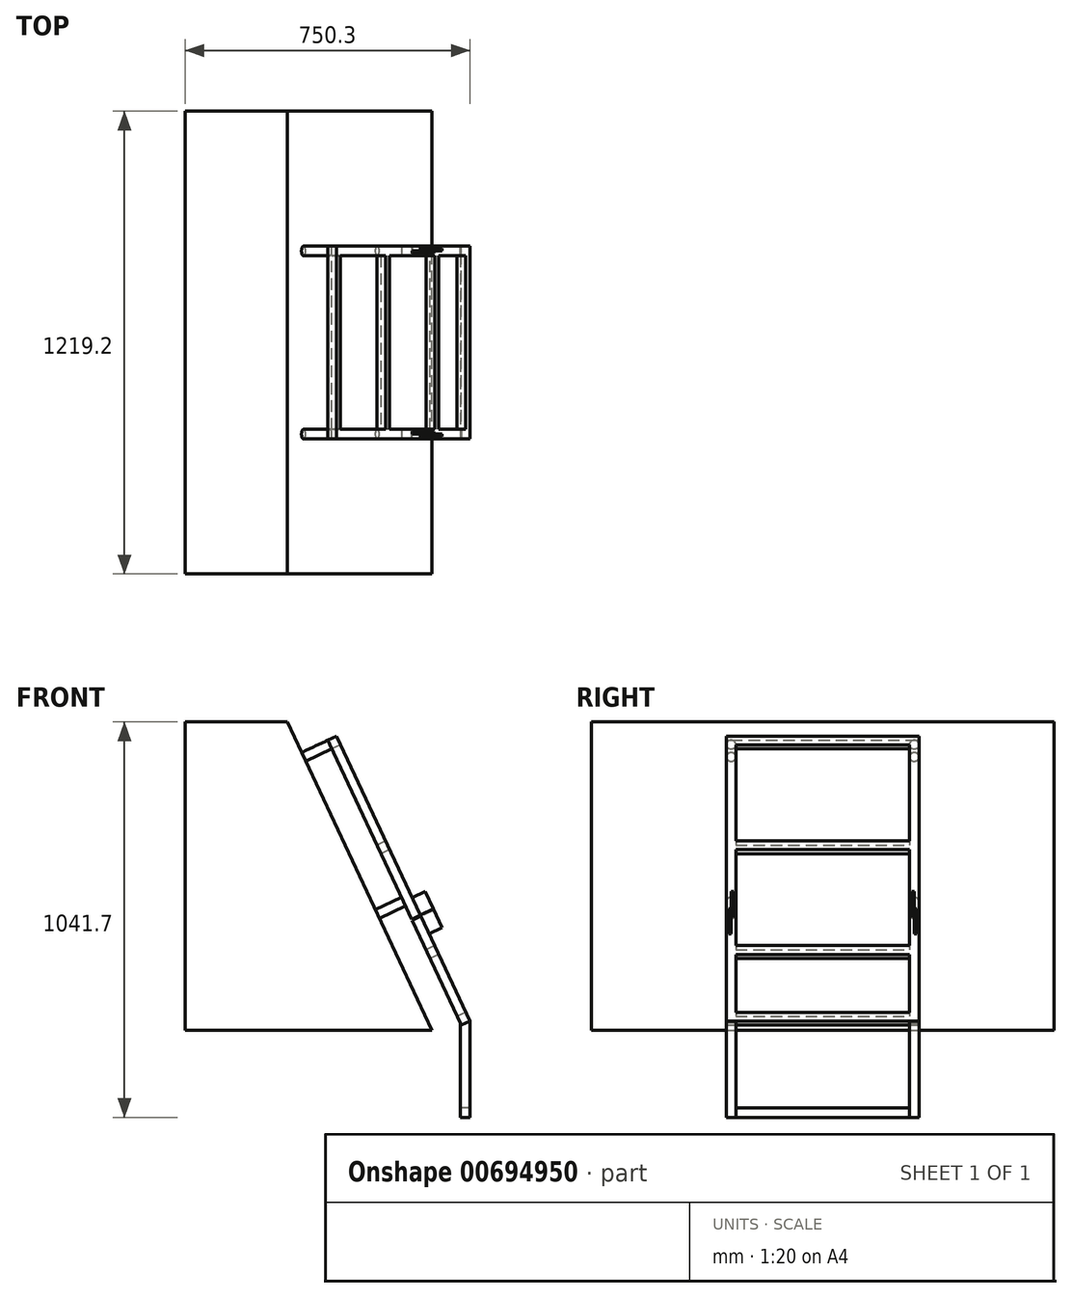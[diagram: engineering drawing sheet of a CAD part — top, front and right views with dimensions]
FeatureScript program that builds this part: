
annotation { "Feature Type Name" : "Feature", "Feature Type Description" : "" }
export const myFeature = defineFeature(function(context is Context, id is Id, definition is map)
    precondition{}
    {
        {
            var Q0;
            Q0=qCreatedBy(makeId("Front.planeOp"),FACE);
            var sketch = newSketch(context, id + "F0", { "sketchPlane" : qUnion([Q0])});
            skLineSegment(sketch, "E0", {"start": v(0, 0) * mm, "end": v(0, 812.8) * mm});
            skLineSegment(sketch, "E1", {"start": v(0, 812.8) * mm, "end": v(-381, 812.8) * mm});
            skLineSegment(sketch, "E2", {"start": v(-381, 812.8) * mm, "end": v(0, 0) * mm});
            skLineSegment(sketch, "E3", {"start": v(0, 0) * mm, "end": v(0, -325.78) * mm});
            skLineSegment(sketch, "E4", {"start": v(-381, 812.8) * mm, "end": v(-649.86, 812.8) * mm});
            skLineSegment(sketch, "E5", {"start": v(-649.86, 812.8) * mm, "end": v(-649.86, 0) * mm});
            skLineSegment(sketch, "E6", {"start": v(-649.86, 0) * mm, "end": v(0, 0) * mm});
            skSolve(sketch);
        }
        {
            var Q0;
            Q0=makeQuery(id+"F0.imprint","IMPRINT",FACE,{"disambiguationData":[TD([[makeQuery(id+"F0.imprint","IMPRINT",EDGE,{"derivedFrom":sQuery(id+"F0.wireOp",EDGE,"E2")}),-1.0]])]});
            extrude(context, id + "F1", {"entities" : qUnion([Q0]), "endBound" : BoundingType.SYMMETRIC, "depth" : 1219.2 * mm, "offsetDistance" : 25.4 * mm});
        }
        {
            var Q0;
            Q0=makeQuery(id+"F1.opExtrude","SWEPT_FACE",FACE,{"disambiguationData":[OSD([sQuery(id+"F0.wireOp",EDGE,"E2")])]});
            var sketch = newSketch(context, id + "F2", { "sketchPlane" : qUnion([Q0])});
            skCircle(sketch, "E7", {"center": v(-241.3, 796.07) * mm, "radius": 12.7 * mm});
            skCircle(sketch, "E8", {"center": v(241.3, 796.07) * mm, "radius": 12.7 * mm});
            skCircle(sketch, "E9", {"center": v(-241.3, 338.87) * mm, "radius": 12.7 * mm});
            skCircle(sketch, "E10", {"center": v(241.3, 338.87) * mm, "radius": 12.7 * mm});
            skSolve(sketch);
        }
        {
            var Q0;
            Q0=makeQuery(id+"F2.imprint","IMPRINT",FACE,{"disambiguationData":[TD([[makeQuery(id+"F2.imprint","IMPRINT",EDGE,{"derivedFrom":sQuery(id+"F2.wireOp",EDGE,"E7")}),1.0]])]});
            var Q1;
            Q1=makeQuery(id+"F2.imprint","IMPRINT",FACE,{"disambiguationData":[TD([[makeQuery(id+"F2.imprint","IMPRINT",EDGE,{"derivedFrom":sQuery(id+"F2.wireOp",EDGE,"E8")}),1.0]])]});
            var Q2;
            Q2=makeQuery(id+"F2.imprint","IMPRINT",FACE,{"disambiguationData":[TD([[makeQuery(id+"F2.imprint","IMPRINT",EDGE,{"derivedFrom":sQuery(id+"F2.wireOp",EDGE,"E10")}),1.0]])]});
            var Q3;
            Q3=makeQuery(id+"F2.imprint","IMPRINT",FACE,{"disambiguationData":[TD([[makeQuery(id+"F2.imprint","IMPRINT",EDGE,{"derivedFrom":sQuery(id+"F2.wireOp",EDGE,"E9")}),1.0]])]});
            extrude(context, id + "F3", {"entities" : qUnion([Q0, Q1, Q2, Q3]), "operationType" : NewBodyOperationType.ADD, "depth" : 76.2 * mm, "offsetDistance" : 25.4 * mm});
        }
        {
            var Q0;
            Q0=makeQuery(id+"F3.opExtrude","CAP_FACE",FACE,{"disambiguationData":[OSD([sQuery(id+"F2.wireOp",EDGE,"E9")])],"isStart":false});
            var sketch = newSketch(context, id + "F4", { "sketchPlane" : qUnion([Q0])});
            skCircle(sketch, "E11.0", {"center": v(-241.3, 796.07) * mm, "radius": 12.7 * mm});
            skCircle(sketch, "E12.0", {"center": v(241.3, 796.07) * mm, "radius": 12.7 * mm});
            skCircle(sketch, "E13.0.0", {"center": v(241.3, 338.87) * mm, "radius": 12.7 * mm});
            skLineSegment(sketch, "E14", {"start": v(-241.3, 796.07) * mm, "end": v(-241.3, 288.07) * mm});
            skLineSegment(sketch, "E15", {"start": v(-241.3, 796.07) * mm, "end": v(241.3, 796.07) * mm});
            skLineSegment(sketch, "E16", {"start": v(241.3, 796.07) * mm, "end": v(241.3, 288.07) * mm});
            skLineSegment(sketch, "E17.0", {"start": v(-254, 808.77) * mm, "end": v(-254, 288.07) * mm});
            skLineSegment(sketch, "E17.1", {"start": v(-254, 808.77) * mm, "end": v(254, 808.77) * mm});
            skLineSegment(sketch, "E17.2", {"start": v(254, 808.77) * mm, "end": v(254, 288.07) * mm});
            skLineSegment(sketch, "E18.0", {"start": v(-228.6, 783.37) * mm, "end": v(-228.6, 288.07) * mm});
            skLineSegment(sketch, "E18.1", {"start": v(-228.6, 783.37) * mm, "end": v(228.6, 783.37) * mm});
            skLineSegment(sketch, "E18.2", {"start": v(228.6, 783.37) * mm, "end": v(228.6, 288.07) * mm});
            skLineSegment(sketch, "E19", {"start": v(-254, 288.07) * mm, "end": v(-228.6, 288.07) * mm});
            skLineSegment(sketch, "E20", {"start": v(254, 288.07) * mm, "end": v(228.6, 288.07) * mm});
            skLineSegment(sketch, "E21", {"start": v(-228.6, 503.97) * mm, "end": v(228.6, 503.97) * mm});
            skLineSegment(sketch, "E22", {"start": v(228.6, 503.97) * mm, "end": v(228.6, 478.57) * mm});
            skLineSegment(sketch, "E23", {"start": v(228.6, 478.57) * mm, "end": v(-228.6, 478.57) * mm});
            skLineSegment(sketch, "E24", {"start": v(-228.6, 478.57) * mm, "end": v(-228.6, 503.97) * mm});
            skLineSegment(sketch, "E25", {"start": v(-254, 284.9) * mm, "end": v(-228.6, 284.9) * mm});
            skLineSegment(sketch, "E26", {"start": v(-228.6, 284.9) * mm, "end": v(-228.6, -19.9) * mm});
            skLineSegment(sketch, "E27", {"start": v(-254, 284.9) * mm, "end": v(-254, -19.9) * mm});
            skLineSegment(sketch, "E28", {"start": v(-254, -19.9) * mm, "end": v(-228.6, -19.9) * mm});
            skLineSegment(sketch, "E29.bottom", {"start": v(254, 284.9) * mm, "end": v(228.6, 284.9) * mm});
            skLineSegment(sketch, "E29.top", {"start": v(254, -19.9) * mm, "end": v(228.6, -19.9) * mm});
            skLineSegment(sketch, "E29.left", {"start": v(254, 284.9) * mm, "end": v(254, -19.9) * mm});
            skLineSegment(sketch, "E29.right", {"start": v(228.6, 284.9) * mm, "end": v(228.6, -19.9) * mm});
            skLineSegment(sketch, "E30.bottom", {"start": v(-228.6, 199.17) * mm, "end": v(228.6, 199.17) * mm});
            skLineSegment(sketch, "E30.top", {"start": v(-228.6, 173.77) * mm, "end": v(228.6, 173.77) * mm});
            skLineSegment(sketch, "E30.left", {"start": v(-228.6, 199.17) * mm, "end": v(-228.6, 173.77) * mm});
            skLineSegment(sketch, "E30.right", {"start": v(228.6, 199.17) * mm, "end": v(228.6, 173.77) * mm});
            skLineSegment(sketch, "E31.bottom", {"start": v(-228.6, -19.9) * mm, "end": v(228.6, -19.9) * mm});
            skLineSegment(sketch, "E31.top", {"start": v(-228.6, 5.5) * mm, "end": v(228.6, 5.5) * mm});
            skLineSegment(sketch, "E31.left", {"start": v(-228.6, -19.9) * mm, "end": v(-228.6, 5.5) * mm});
            skLineSegment(sketch, "E31.right", {"start": v(228.6, -19.9) * mm, "end": v(228.6, 5.5) * mm});
            skSolve(sketch);
        }
        {
            var Q0;
            {var subQ5=sQuery(id+"F4.wireOp",EDGE,"E18.1");Q0=makeQuery(id+"F4.imprint","IMPRINT",FACE,{"disambiguationData":[TD([[makeQuery(id+"F4.imprint","IMPRINT",EDGE,{"derivedFrom":subQ5}),1.0]])]});}
            var Q1;
            {var subQ0=sQuery(id+"F4.wireOp",EDGE,"E17.1");var subQ1=sQuery(id+"F4.wireOp",EDGE,"E11.0");var subQ2=makeQuery(id+"F4.imprint","INTERSECT",VERTEX,{"derivedFrom":[subQ1,subQ0]});Q1=makeQuery(id+"F4.imprint","IMPRINT",FACE,{"disambiguationData":[TD([[makeQuery(id+"F4.imprint","IMPRINT",EDGE,{"disambiguationData":[TD([[subQ2,1.0]])],"derivedFrom":subQ1}),-1.0]])]});}
            var Q2;
            {var subQ0=sQuery(id+"F4.wireOp",EDGE,"E17.0");var subQ1=sQuery(id+"F4.wireOp",EDGE,"E11.0");var subQ2=makeQuery(id+"F4.imprint","INTERSECT",VERTEX,{"derivedFrom":[subQ1,subQ0]});Q2=makeQuery(id+"F4.imprint","IMPRINT",FACE,{"disambiguationData":[TD([[makeQuery(id+"F4.imprint","IMPRINT",EDGE,{"disambiguationData":[TD([[subQ2,-1.0]])],"derivedFrom":subQ1}),-1.0]])]});}
            var Q3;
            {var subQ0=sQuery(id+"F4.wireOp",EDGE,"E17.2");var subQ1=sQuery(id+"F4.wireOp",EDGE,"E12.0");var subQ2=makeQuery(id+"F4.imprint","INTERSECT",VERTEX,{"derivedFrom":[subQ1,subQ0]});Q3=makeQuery(id+"F4.imprint","IMPRINT",FACE,{"disambiguationData":[TD([[makeQuery(id+"F4.imprint","IMPRINT",EDGE,{"disambiguationData":[TD([[subQ2,1.0]])],"derivedFrom":subQ1}),-1.0]])]});}
            var Q4;
            {var subQ3=sQuery(id+"F4.wireOp",EDGE,"E12.0");var subQ7=makeQuery(id+"F4.imprint","INTERSECT",VERTEX,{"derivedFrom":[subQ3,sQuery(id+"F4.wireOp",EDGE,"E17.1")]});Q4=makeQuery(id+"F4.imprint","IMPRINT",FACE,{"disambiguationData":[TD([[makeQuery(id+"F4.imprint","IMPRINT",EDGE,{"disambiguationData":[TD([[subQ7,1.0]])],"derivedFrom":subQ3}),1.0]])]});}
            var Q5;
            {var subQ0=sQuery(id+"F4.wireOp",EDGE,"E15");var subQ1=sQuery(id+"F4.wireOp",EDGE,"E12.0");var subQ2=makeQuery(id+"F4.imprint","INTERSECT",VERTEX,{"derivedFrom":[subQ1,subQ0]});Q5=makeQuery(id+"F4.imprint","IMPRINT",FACE,{"disambiguationData":[TD([[makeQuery(id+"F4.imprint","IMPRINT",EDGE,{"disambiguationData":[TD([[subQ2,-1.0]])],"derivedFrom":subQ1}),1.0]])]});}
            var Q6;
            {var subQ0=sQuery(id+"F4.wireOp",EDGE,"E17.1");var subQ1=sQuery(id+"F4.wireOp",EDGE,"E12.0");var subQ2=makeQuery(id+"F4.imprint","INTERSECT",VERTEX,{"derivedFrom":[subQ1,subQ0]});Q6=makeQuery(id+"F4.imprint","IMPRINT",FACE,{"disambiguationData":[TD([[makeQuery(id+"F4.imprint","IMPRINT",EDGE,{"disambiguationData":[TD([[subQ2,1.0]])],"derivedFrom":subQ1}),-1.0]])]});}
            var Q7;
            {var subQ3=sQuery(id+"F4.wireOp",EDGE,"E11.0");var subQ5=makeQuery(id+"F4.imprint","INTERSECT",VERTEX,{"derivedFrom":[subQ3,sQuery(id+"F4.wireOp",EDGE,"E17.1")]});Q7=makeQuery(id+"F4.imprint","IMPRINT",FACE,{"disambiguationData":[TD([[makeQuery(id+"F4.imprint","IMPRINT",EDGE,{"disambiguationData":[TD([[subQ5,1.0]])],"derivedFrom":subQ3}),1.0]])]});}
            var Q8;
            {var subQ0=sQuery(id+"F4.wireOp",EDGE,"E17.1");var subQ1=sQuery(id+"F4.wireOp",EDGE,"E11.0");var subQ2=makeQuery(id+"F4.imprint","INTERSECT",VERTEX,{"derivedFrom":[subQ1,subQ0]});Q8=makeQuery(id+"F4.imprint","IMPRINT",FACE,{"disambiguationData":[TD([[makeQuery(id+"F4.imprint","IMPRINT",EDGE,{"disambiguationData":[TD([[subQ2,-1.0]])],"derivedFrom":subQ1}),-1.0]])]});}
            var Q9;
            {var subQ0=sQuery(id+"F4.wireOp",EDGE,"E15");var subQ1=sQuery(id+"F4.wireOp",EDGE,"E11.0");var subQ2=makeQuery(id+"F4.imprint","INTERSECT",VERTEX,{"derivedFrom":[subQ1,subQ0]});Q9=makeQuery(id+"F4.imprint","IMPRINT",FACE,{"disambiguationData":[TD([[makeQuery(id+"F4.imprint","IMPRINT",EDGE,{"disambiguationData":[TD([[subQ2,1.0]])],"derivedFrom":subQ1}),1.0]])]});}
            var Q10;
            Q10=makeQuery(id+"F4.imprint","IMPRINT",FACE,{"disambiguationData":[TD([[makeQuery(id+"F4.imprint","IMPRINT",EDGE,{"derivedFrom":sQuery(id+"F4.wireOp",EDGE,"E21")}),-1.0]])]});
            var Q11;
            {var subQ0=sQuery(id+"F4.wireOp",EDGE,"E14");var subQ1=makeQuery(id+"F3.opExtrude","CAP_EDGE",EDGE,{"disambiguationData":[OSD([sQuery(id+"F2.wireOp",EDGE,"E9")])],"isStart":false});var subQ2=makeQuery(id+"F4.imprint","INTERSECT",VERTEX,{"disambiguationData":[OD(0.0)],"derivedFrom":[subQ1,subQ0]});Q11=makeQuery(id+"F4.imprint","IMPRINT",FACE,{"disambiguationData":[TD([[makeQuery(id+"F4.imprint","IMPRINT",EDGE,{"disambiguationData":[TD([[subQ2,-1.0]])],"derivedFrom":subQ0}),-1.0]])]});}
            var Q12;
            {var subQ0=sQuery(id+"F4.wireOp",EDGE,"E14");var subQ1=makeQuery(id+"F3.opExtrude","CAP_EDGE",EDGE,{"disambiguationData":[OSD([sQuery(id+"F2.wireOp",EDGE,"E9")])],"isStart":false});var subQ2=makeQuery(id+"F4.imprint","INTERSECT",VERTEX,{"disambiguationData":[OD(0.0)],"derivedFrom":[subQ1,subQ0]});Q12=makeQuery(id+"F4.imprint","IMPRINT",FACE,{"disambiguationData":[TD([[makeQuery(id+"F4.imprint","IMPRINT",EDGE,{"disambiguationData":[TD([[subQ2,-1.0]])],"derivedFrom":subQ0}),1.0]])]});}
            var Q13;
            {var subQ0=sQuery(id+"F4.wireOp",EDGE,"E19");var subQ1=sQuery(id+"F4.wireOp",EDGE,"E14");var subQ2=makeQuery(id+"F4.imprint","INTERSECT",VERTEX,{"derivedFrom":[subQ1,subQ0]});Q13=makeQuery(id+"F4.imprint","IMPRINT",FACE,{"disambiguationData":[TD([[makeQuery(id+"F4.imprint","IMPRINT",EDGE,{"disambiguationData":[TD([[subQ2,1.0]])],"derivedFrom":subQ1}),1.0]])]});}
            var Q14;
            {var subQ0=sQuery(id+"F4.wireOp",EDGE,"E19");var subQ1=sQuery(id+"F4.wireOp",EDGE,"E14");var subQ2=makeQuery(id+"F4.imprint","INTERSECT",VERTEX,{"derivedFrom":[subQ1,subQ0]});Q14=makeQuery(id+"F4.imprint","IMPRINT",FACE,{"disambiguationData":[TD([[makeQuery(id+"F4.imprint","IMPRINT",EDGE,{"disambiguationData":[TD([[subQ2,1.0]])],"derivedFrom":subQ1}),-1.0]])]});}
            var Q15;
            {var subQ3=sQuery(id+"F4.wireOp",EDGE,"E25");Q15=makeQuery(id+"F4.imprint","IMPRINT",FACE,{"disambiguationData":[TD([[makeQuery(id+"F4.imprint","IMPRINT",EDGE,{"derivedFrom":subQ3}),-1.0]])]});}
            var Q16;
            {var subQ0=sQuery(id+"F4.wireOp",EDGE,"E13.0.0");var subQ1=makeQuery(id+"F4.imprint","INTERSECT",VERTEX,{"derivedFrom":[subQ0,sQuery(id+"F4.wireOp",EDGE,"E17.2")]});Q16=makeQuery(id+"F4.imprint","IMPRINT",FACE,{"disambiguationData":[TD([[makeQuery(id+"F4.imprint","IMPRINT",EDGE,{"disambiguationData":[TD([[subQ1,-1.0]])],"derivedFrom":subQ0}),1.0]])]});}
            var Q17;
            {var subQ0=sQuery(id+"F4.wireOp",EDGE,"E13.0.0");var subQ1=makeQuery(id+"F4.imprint","INTERSECT",VERTEX,{"derivedFrom":[subQ0,sQuery(id+"F4.wireOp",EDGE,"E18.2")]});Q17=makeQuery(id+"F4.imprint","IMPRINT",FACE,{"disambiguationData":[TD([[makeQuery(id+"F4.imprint","IMPRINT",EDGE,{"disambiguationData":[TD([[subQ1,1.0]])],"derivedFrom":subQ0}),1.0]])]});}
            var Q18;
            {var subQ0=sQuery(id+"F4.wireOp",EDGE,"E18.2");var subQ1=sQuery(id+"F4.wireOp",EDGE,"E13.0.0");var subQ2=makeQuery(id+"F4.imprint","INTERSECT",VERTEX,{"derivedFrom":[subQ1,subQ0]});Q18=makeQuery(id+"F4.imprint","IMPRINT",FACE,{"disambiguationData":[TD([[makeQuery(id+"F4.imprint","IMPRINT",EDGE,{"disambiguationData":[TD([[subQ2,-1.0]])],"derivedFrom":subQ1}),-1.0]])]});}
            var Q19;
            {var subQ0=sQuery(id+"F4.wireOp",EDGE,"E17.2");var subQ1=sQuery(id+"F4.wireOp",EDGE,"E13.0.0");var subQ2=makeQuery(id+"F4.imprint","INTERSECT",VERTEX,{"derivedFrom":[subQ1,subQ0]});Q19=makeQuery(id+"F4.imprint","IMPRINT",FACE,{"disambiguationData":[TD([[makeQuery(id+"F4.imprint","IMPRINT",EDGE,{"disambiguationData":[TD([[subQ2,1.0]])],"derivedFrom":subQ1}),-1.0]])]});}
            var Q20;
            {var subQ1=sQuery(id+"F4.wireOp",EDGE,"E29.bottom");Q20=makeQuery(id+"F4.imprint","IMPRINT",FACE,{"disambiguationData":[TD([[makeQuery(id+"F4.imprint","IMPRINT",EDGE,{"derivedFrom":subQ1}),1.0]])]});}
            var Q21;
            Q21=makeQuery(id+"F4.imprint","IMPRINT",FACE,{"disambiguationData":[TD([[makeQuery(id+"F4.imprint","IMPRINT",EDGE,{"derivedFrom":sQuery(id+"F4.wireOp",EDGE,"E30.bottom")}),-1.0]])]});
            var Q22;
            Q22=makeQuery(id+"F4.imprint","IMPRINT",FACE,{"disambiguationData":[TD([[makeQuery(id+"F4.imprint","IMPRINT",EDGE,{"derivedFrom":sQuery(id+"F4.wireOp",EDGE,"E31.bottom")}),1.0]])]});
            extrude(context, id + "F5", {"entities" : qUnion([Q0, Q1, Q2, Q3, Q4, Q5, Q6, Q7, Q8, Q9, Q10, Q11, Q12, Q13, Q14, Q15, Q16, Q17, Q18, Q19, Q20, Q21, Q22]), "operationType" : NewBodyOperationType.ADD, "depth" : 25.4 * mm, "offsetDistance" : 25.4 * mm});
        }
        {
            var Q0;
            Q0=makeQuery(id+"F5.opExtrude","SWEPT_FACE",FACE,{"disambiguationData":[OSD([sQuery(id+"F4.wireOp",EDGE,"E27")])]});
            var sketch = newSketch(context, id + "F6", { "sketchPlane" : qUnion([Q0])});
            skLineSegment(sketch, "E32", {"start": v(100.44, 25.1) * mm, "end": v(100.44, -228.9) * mm});
            skLineSegment(sketch, "E33", {"start": v(75.04, -228.9) * mm, "end": v(100.44, -228.9) * mm});
            skLineSegment(sketch, "E34", {"start": v(75.04, -228.9) * mm, "end": v(75.04, 19.44) * mm});
            skSolve(sketch);
        }
        {
            var Q0;
            Q0=makeQuery(id+"F6.imprint","IMPRINT",FACE,{"disambiguationData":[TD([[makeQuery(id+"F6.imprint","IMPRINT",EDGE,{"derivedFrom":sQuery(id+"F6.wireOp",EDGE,"E32")}),-1.0]])]});
            extrude(context, id + "F7", {"entities" : qUnion([Q0]), "oppositeDirection" : true, "depth" : 25.4 * mm, "offsetDistance" : 25.4 * mm});
        }
        {
            var Q0;
            Q0=makeQuery(id+"F5.opExtrude","SWEPT_FACE",FACE,{"disambiguationData":[OSD([sQuery(id+"F4.wireOp",EDGE,"E29.left")])]});
            var sketch = newSketch(context, id + "F8", { "sketchPlane" : qUnion([Q0])});
            skLineSegment(sketch, "E35", {"start": v(-100.44, 25.1) * mm, "end": v(-100.44, -228.9) * mm});
            skLineSegment(sketch, "E36", {"start": v(-100.44, -228.9) * mm, "end": v(-75.04, -228.9) * mm});
            skLineSegment(sketch, "E37", {"start": v(-75.04, -228.9) * mm, "end": v(-75.04, 19.44) * mm});
            skSolve(sketch);
        }
        {
            var Q0;
            Q0=makeQuery(id+"F8.imprint","IMPRINT",FACE,{"disambiguationData":[TD([[makeQuery(id+"F8.imprint","IMPRINT",EDGE,{"derivedFrom":sQuery(id+"F8.wireOp",EDGE,"E35")}),1.0]])]});
            extrude(context, id + "F9", {"entities" : qUnion([Q0]), "oppositeDirection" : true, "depth" : 25.4 * mm, "offsetDistance" : 25.4 * mm});
        }
        {
            var Q0;
            Q0=makeQuery(id+"F7.opExtrude","CAP_FACE",FACE,{"disambiguationData":[OSD([sQuery(id+"F4.wireOp",EDGE,"E27"),sQuery(id+"F4.wireOp",EDGE,"E28"),sQuery(id+"F6.wireOp",EDGE,"E32"),sQuery(id+"F6.wireOp",EDGE,"E33"),sQuery(id+"F6.wireOp",EDGE,"E34")])],"isStart":false});
            var sketch = newSketch(context, id + "F10", { "sketchPlane" : qUnion([Q0])});
            skLineSegment(sketch, "E38.bottom", {"start": v(-100.44, -228.9) * mm, "end": v(-75.04, -228.9) * mm});
            skLineSegment(sketch, "E38.top", {"start": v(-100.44, -203.5) * mm, "end": v(-75.04, -203.5) * mm});
            skLineSegment(sketch, "E38.left", {"start": v(-100.44, -228.9) * mm, "end": v(-100.44, -203.5) * mm});
            skLineSegment(sketch, "E38.right", {"start": v(-75.04, -228.9) * mm, "end": v(-75.04, -203.5) * mm});
            skSolve(sketch);
        }
        {
            var Q0;
            Q0=makeQuery(id+"F10.imprint","IMPRINT",FACE,{"disambiguationData":[TD([[makeQuery(id+"F10.imprint","IMPRINT",EDGE,{"derivedFrom":sQuery(id+"F10.wireOp",EDGE,"E38.bottom")}),-1.0]])]});
            extrude(context, id + "F11", {"entities" : qUnion([Q0]), "endBound" : BoundingType.UP_TO_NEXT, "depth" : 25.4 * mm, "offsetDistance" : 25.4 * mm});
        }
        {
            var Q0;
            Q0=makeQuery(id+"F5.opExtrude","CAP_FACE",FACE,{"disambiguationData":[OSD([sQuery(id+"F4.wireOp",EDGE,"E25"),sQuery(id+"F4.wireOp",EDGE,"E26"),sQuery(id+"F4.wireOp",EDGE,"E27"),sQuery(id+"F4.wireOp",EDGE,"E28"),sQuery(id+"F4.wireOp",EDGE,"E29.bottom"),sQuery(id+"F4.wireOp",EDGE,"E29.top"),sQuery(id+"F4.wireOp",EDGE,"E29.left"),sQuery(id+"F4.wireOp",EDGE,"E29.right"),sQuery(id+"F4.wireOp",EDGE,"E30.bottom"),sQuery(id+"F4.wireOp",EDGE,"E30.top"),sQuery(id+"F4.wireOp",EDGE,"E31.bottom"),sQuery(id+"F4.wireOp",EDGE,"E31.top")])],"isStart":false});
            var sketch = newSketch(context, id + "F12", { "sketchPlane" : qUnion([Q0])});
            skLineSegment(sketch, "E39.bottom", {"start": v(-247.65, 234.1) * mm, "end": v(-241.3, 234.1) * mm});
            skLineSegment(sketch, "E39.top", {"start": v(-247.65, 288.07) * mm, "end": v(-241.3, 288.07) * mm});
            skLineSegment(sketch, "E39.left", {"start": v(-247.65, 234.1) * mm, "end": v(-247.65, 288.07) * mm});
            skLineSegment(sketch, "E39.right", {"start": v(-241.3, 234.1) * mm, "end": v(-241.3, 288.07) * mm});
            skLineSegment(sketch, "E40.bottom", {"start": v(-241.3, 284.9) * mm, "end": v(-234.95, 284.9) * mm});
            skLineSegment(sketch, "E40.top", {"start": v(-241.3, 338.87) * mm, "end": v(-234.95, 338.87) * mm});
            skLineSegment(sketch, "E40.left", {"start": v(-241.3, 284.9) * mm, "end": v(-241.3, 338.87) * mm});
            skLineSegment(sketch, "E40.right", {"start": v(-234.95, 284.9) * mm, "end": v(-234.95, 338.87) * mm});
            skLineSegment(sketch, "E41.bottom", {"start": v(247.65, 234.1) * mm, "end": v(241.3, 234.1) * mm});
            skLineSegment(sketch, "E41.top", {"start": v(247.65, 288.07) * mm, "end": v(241.3, 288.07) * mm});
            skLineSegment(sketch, "E41.left", {"start": v(247.65, 234.1) * mm, "end": v(247.65, 288.07) * mm});
            skLineSegment(sketch, "E41.right", {"start": v(241.3, 234.1) * mm, "end": v(241.3, 288.07) * mm});
            skLineSegment(sketch, "E42.bottom", {"start": v(241.3, 284.9) * mm, "end": v(234.95, 284.9) * mm});
            skLineSegment(sketch, "E42.top", {"start": v(241.3, 338.87) * mm, "end": v(234.95, 338.87) * mm});
            skLineSegment(sketch, "E42.left", {"start": v(241.3, 284.9) * mm, "end": v(241.3, 338.87) * mm});
            skLineSegment(sketch, "E42.right", {"start": v(234.95, 284.9) * mm, "end": v(234.95, 338.87) * mm});
            skSolve(sketch);
        }
        {
            var Q0;
            {var subQ3=sQuery(id+"F12.wireOp",EDGE,"E40.bottom");Q0=makeQuery(id+"F12.imprint","IMPRINT",FACE,{"disambiguationData":[TD([[makeQuery(id+"F12.imprint","IMPRINT",EDGE,{"derivedFrom":subQ3}),1.0]])]});}
            var Q1;
            {var subQ0=sQuery(id+"F12.wireOp",EDGE,"E39.bottom");Q1=makeQuery(id+"F12.imprint","IMPRINT",FACE,{"disambiguationData":[TD([[makeQuery(id+"F12.imprint","IMPRINT",EDGE,{"derivedFrom":subQ0}),1.0]])]});}
            var Q2;
            {var subQ0=sQuery(id+"F12.wireOp",EDGE,"E39.top");Q2=makeQuery(id+"F12.imprint","IMPRINT",FACE,{"disambiguationData":[TD([[makeQuery(id+"F12.imprint","IMPRINT",EDGE,{"derivedFrom":subQ0}),-1.0]])]});}
            var Q3;
            {var subQ0=sQuery(id+"F12.wireOp",EDGE,"E41.bottom");Q3=makeQuery(id+"F12.imprint","IMPRINT",FACE,{"disambiguationData":[TD([[makeQuery(id+"F12.imprint","IMPRINT",EDGE,{"derivedFrom":subQ0}),-1.0]])]});}
            var Q4;
            {var subQ0=sQuery(id+"F12.wireOp",EDGE,"E41.top");Q4=makeQuery(id+"F12.imprint","IMPRINT",FACE,{"disambiguationData":[TD([[makeQuery(id+"F12.imprint","IMPRINT",EDGE,{"derivedFrom":subQ0}),1.0]])]});}
            var Q5;
            {var subQ3=sQuery(id+"F12.wireOp",EDGE,"E42.bottom");Q5=makeQuery(id+"F12.imprint","IMPRINT",FACE,{"disambiguationData":[TD([[makeQuery(id+"F12.imprint","IMPRINT",EDGE,{"derivedFrom":subQ3}),-1.0]])]});}
            extrude(context, id + "F13", {"entities" : qUnion([Q0, Q1, Q2, Q3, Q4, Q5]), "depth" : 38.1 * mm, "offsetDistance" : 25.4 * mm});
        }
    });
